# Revit family: RAV_GM1ATP_160_Outdoor Unit
name_source: partatom
category: Mechanical Equipment
revit_build: Autodesk Revit 2017 (Build: 20160225_1515(x64)
units: mm (PartAtom-declared; Revit-internal decimal feet)

## family parameters
Always vertical = Yes
Cut with Voids When Loaded = No
OmniClass Number = 23.75.00.00
OmniClass Title = Climate Control (HVAC)
Part Type = Normal
Room Calculation Point = No
Round Connector Dimension = Use Diameter
Shared = No
Work Plane-Based = No

## types (2) — shared parameters
Airflow m3/h-Cooling/Heating = 6900
Article Description = R32 DI
Compressor detail - Motor output  (KW) = -
Compressor detail - Type = Hermetic twin rotary compressor
Content Supplier URL = www.hcltech.com
Custom = No
Depth (mm) = 320 mm  [stored 1.04987 ft]
Description = R32 DI
Drain pipe(mm) = -
Duct diameters(mm) = -
EMCS = 4
ETIM Article Class = EC001213
Energy class-Cooling/Heating = -
Height (mm) = 1340 mm  [stored 4.39633 ft]
MCA (A) = -
MEPcontent Class = HEATPUMP
Manufacturer = Toshiba
Manufacturer URL = https://www.toshiba-carrier.co.jp
Operating range - Cooling (°C) = -15 to 46
Pdesigh-Cooling/Heating = -
Piping diameter (mm)-Gas = 16 mm
Piping diameter (mm)-Liquid = 10 mm  [stored 0.0328084 ft]
Power consumption-Cooling = -
Power consumption-Heating = -
Product Line = TCTC
Rated Capacity kW-Cooling/Heating = -
Rated Power Consumption kW-Cooling/Heating = -
Rated efficiency-EER / COP = -
Red = Colour RGB-250 000 000
Refrigerant information = R32
Revit Version = 2017
Running current-Cooling = -
Running current-Heating = -
Seasonal Efficiency-SEER  / SCOP = -
Sound pressure dB(A) - Cooling/Heating-High = 53 / 55
Sound pressure dB(A) - Cooling/Heating-Low = -
Sound pressure dB(A) - Cooling/Heating-Mid = -
Starting current = -
Static pressure = -
URL = https://www.toshiba-carrier.co.jp
Weight (Kg) = -
White = Colour RGB-255 255 255
Width (mm) = 900 mm  [stored 2.95276 ft]

## per-type parameters (varying)
| type | Frequency (Hz) | MOCP (A) | Operating range - Heating (°C) | Voltage (V) |
| RAV-GM1601ATP-E | 50Hz 220-240V | 32 | -20 to 15 | 60Hz 220V |
| RAV-GM1601AT8P-E | 3Phase 50Hz 380-415V | 20 | -15 to 15 | 3Phase 60Hz 380V |

note: column(s) folded — value = type name in every type: Article Type, Manufacturer Art. No., Model

note: [stored X ft] marks values corroborated as IEEE doubles in the binary element streams (Revit-internal decimal feet)

## geometry (parser evidence)
native form markers: Sweep x8
no freeform markers — native parametric forms only
